# Revit family: Haworth_Masters_Bookcase
name_source: partatom
category: Furniture Systems
revit_build: Autodesk Revit 2018 (Build: 20170223_1515(x64)
units: mm (PartAtom-declared; Revit-internal decimal feet)

## family parameters
Always vertical = Yes
Cut with Voids When Loaded = No
OmniClass Number = 23.40.70.14.64.21
OmniClass Title = Systems Furniture
Part Type = Normal
Room Calculation Point = No
Round Connector Dimension = Use Diameter
Shared = No
Work Plane-Based = No

## types (5) — shared parameters
Actual Depth = 14"
Actual Width = 36"
Assembly Code = E2020200
Base Height = 3"
Cabinet Finish = Haworth _ Wood _ White Oak
Description = Haworth - Masters - Bookcase
Legal Depth = No
Letter Depth = Yes
Manufacturer = Haworth
Max. Height = 81 5/8"
Max. Width = 36"
Min. Height = 69"
Min. Width = 30"
Model = Haworth - Masters - Bookcase
Panel Thickness = 3/4"
Revision Number = 2
Shelf Depth = 13 1/4"
Shelf Height 1 = 15"
Shelf Height 2 = 28"
Shelf Height 3 = 41"
Shelf Height 4 = 54"
Shelf Height 5 = 67"
Shelf Width = 34 1/2"
Size = Verify Final Dim. w/ Haworth
Sustainability Info = http://www.haworth.com
URL = www.haworth.com
URL - Product = http://www.haworth.com
Warranty = http://www.haworth.com
Width 30 = No
Width 36 = Yes

## per-type parameters (varying)
| type | Actual Height | Actual Shelf 2 | Actual Shelf 3 | Actual Shelf 4 | Actual Shelf 5 | Five High | Four High | Six High | Three High | Two High |
| Six High - 36w 14d | 81 5/8" | Yes | Yes | Yes | Yes | No | No | Yes | No | No |
| Five High - 36w 14d | 69" | Yes | Yes | Yes | No | Yes | No | No | No | No |
| Four High - 36w 14d | 55 5/16" | Yes | Yes | No | No | No | Yes | No | No | No |
| Three High - 36w 14d | 41 5/8" | Yes | No | No | No | No | No | No | Yes | No |
| Two High - 36w 14d | 28" | No | No | No | No | No | No | No | No | Yes |

## geometry (parser evidence)
native form markers: Sweep x6
no freeform markers — native parametric forms only
